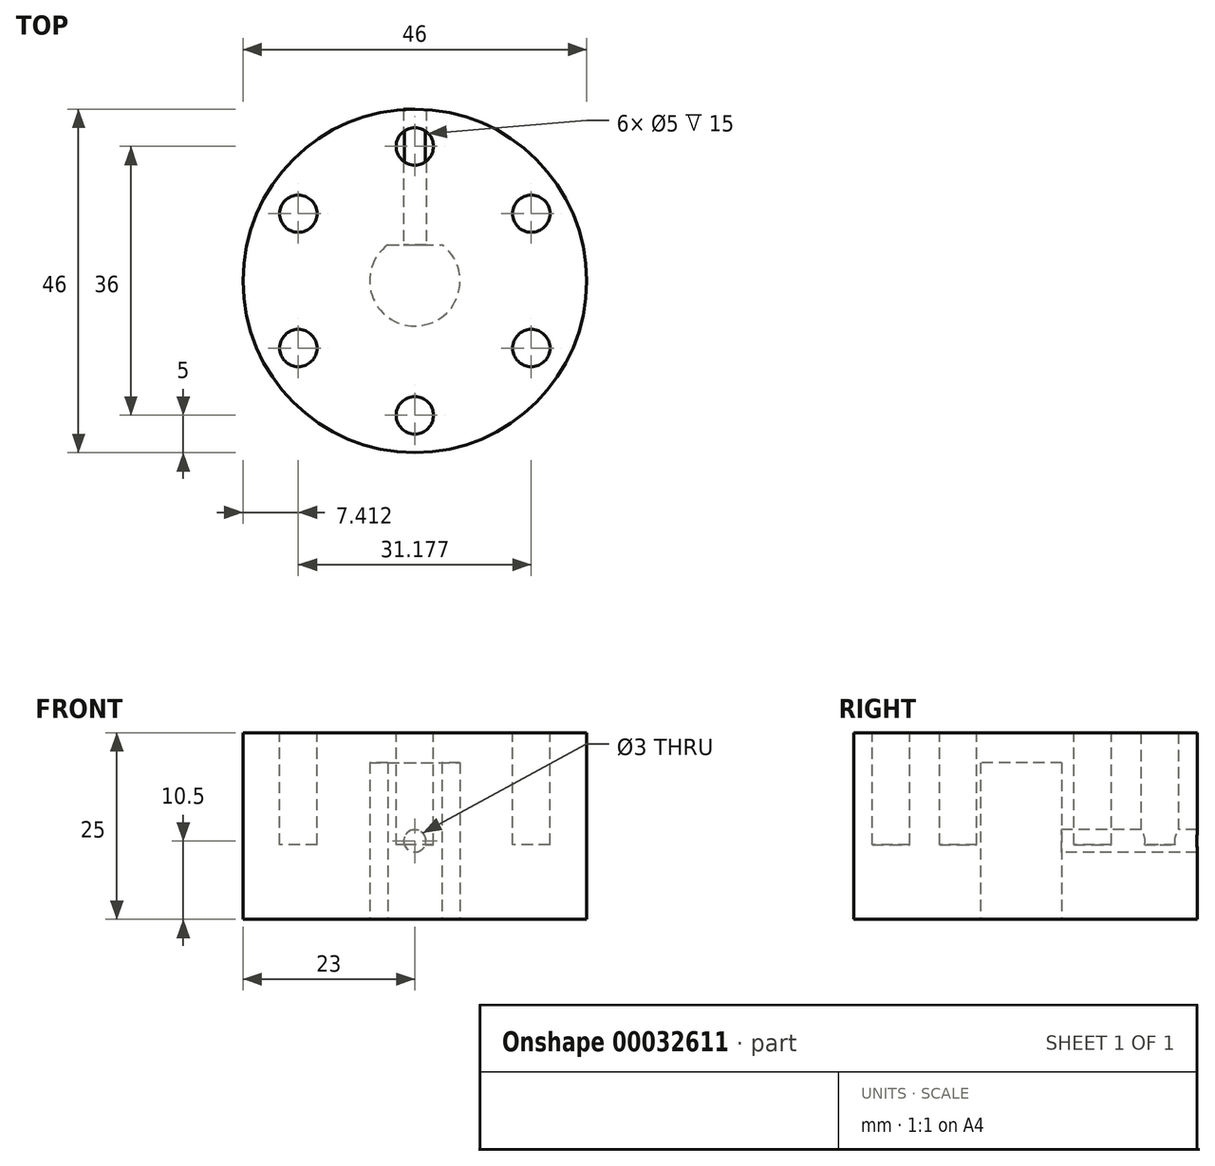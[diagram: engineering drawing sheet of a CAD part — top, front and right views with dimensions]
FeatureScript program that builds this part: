
annotation { "Feature Type Name" : "Feature", "Feature Type Description" : "" }
export const myFeature = defineFeature(function(context is Context, id is Id, definition is map)
    precondition{}
    {
        {
            var Q0;
            Q0=qCreatedBy(makeId("Top.planeOp"),FACE);
            var sketch = newSketch(context, id + "F0", { "sketchPlane" : qUnion([Q0])});
            skCircle(sketch, "E0", {"center": v(0, 0) * mm, "radius": 23 * mm});
            skCircle(sketch, "E1", {"center": v(0, 0) * mm, "radius": 6.05 * mm});
            skLineSegment(sketch, "E2.bottom", {"start": v(-4.85, 4.85) * mm, "end": v(4.85, 4.85) * mm});
            skLineSegment(sketch, "E2.top", {"start": v(-4.85, -4.85) * mm, "end": v(4.85, -4.85) * mm});
            skLineSegment(sketch, "E2.left", {"start": v(-4.85, 4.85) * mm, "end": v(-4.85, -4.85) * mm});
            skLineSegment(sketch, "E2.right", {"start": v(4.85, 4.85) * mm, "end": v(4.85, -4.85) * mm});
            skSolve(sketch);
        }
        {
            var Q0;
            {var subQ5=sQuery(id+"F0.wireOp",EDGE,"9920e3ed-193f-4a9b-bda4-b06f0bd62151.right");Q0=makeQuery(id+"F0.imprint","IMPRINT",FACE,{"disambiguationData":[TD([[makeQuery(id+"F0.imprint","IMPRINT",EDGE,{"derivedFrom":subQ5}),-1.0]])]});}
            var Q1;
            Q1=makeQuery(id+"F0.imprint","IMPRINT",FACE,{"disambiguationData":[TD([[makeQuery(id+"F0.imprint","IMPRINT",EDGE,{"derivedFrom":sQuery(id+"F0.wireOp",EDGE,"E0")}),1.0]])]});
            var Q2;
            {var subQ0=sQuery(id+"F0.wireOp",EDGE,"E2.bottom");var subQ1=sQuery(id+"F0.wireOp",EDGE,"E1");var subQ2=makeQuery(id+"F0.imprint","INTERSECT",VERTEX,{"disambiguationData":[OD(0.0)],"derivedFrom":[subQ1,subQ0]});Q2=makeQuery(id+"F0.imprint","IMPRINT",FACE,{"disambiguationData":[TD([[makeQuery(id+"F0.imprint","IMPRINT",EDGE,{"disambiguationData":[TD([[subQ2,1.0]])],"derivedFrom":subQ1}),-1.0]])]});}
            var Q3;
            {var subQ0=sQuery(id+"F0.wireOp",EDGE,"E2.bottom");var subQ1=sQuery(id+"F0.wireOp",EDGE,"E1");var subQ2=makeQuery(id+"F0.imprint","INTERSECT",VERTEX,{"disambiguationData":[OD(0.0)],"derivedFrom":[subQ1,subQ0]});Q3=makeQuery(id+"F0.imprint","IMPRINT",FACE,{"disambiguationData":[TD([[makeQuery(id+"F0.imprint","IMPRINT",EDGE,{"disambiguationData":[TD([[subQ2,-1.0]])],"derivedFrom":subQ1}),1.0]])]});}
            var Q4;
            {var subQ0=sQuery(id+"F0.wireOp",EDGE,"E2.bottom");var subQ1=sQuery(id+"F0.wireOp",EDGE,"E1");var subQ2=makeQuery(id+"F0.imprint","INTERSECT",VERTEX,{"disambiguationData":[OD(1.0)],"derivedFrom":[subQ1,subQ0]});Q4=makeQuery(id+"F0.imprint","IMPRINT",FACE,{"disambiguationData":[TD([[makeQuery(id+"F0.imprint","IMPRINT",EDGE,{"disambiguationData":[TD([[subQ2,-1.0]])],"derivedFrom":subQ1}),-1.0]])]});}
            var Q5;
            {var subQ0=sQuery(id+"F0.wireOp",EDGE,"E2.left");var subQ1=sQuery(id+"F0.wireOp",EDGE,"E1");var subQ2=makeQuery(id+"F0.imprint","INTERSECT",VERTEX,{"disambiguationData":[OD(1.0)],"derivedFrom":[subQ1,subQ0]});Q5=makeQuery(id+"F0.imprint","IMPRINT",FACE,{"disambiguationData":[TD([[makeQuery(id+"F0.imprint","IMPRINT",EDGE,{"disambiguationData":[TD([[subQ2,-1.0]])],"derivedFrom":subQ1}),-1.0]])]});}
            var Q6;
            {var subQ0=sQuery(id+"F0.wireOp",EDGE,"E2.top");var subQ1=sQuery(id+"F0.wireOp",EDGE,"E1");var subQ2=makeQuery(id+"F0.imprint","INTERSECT",VERTEX,{"disambiguationData":[OD(1.0)],"derivedFrom":[subQ1,subQ0]});Q6=makeQuery(id+"F0.imprint","IMPRINT",FACE,{"disambiguationData":[TD([[makeQuery(id+"F0.imprint","IMPRINT",EDGE,{"disambiguationData":[TD([[subQ2,-1.0]])],"derivedFrom":subQ1}),-1.0]])]});}
            extrude(context, id + "F4", {"entities" : qUnion([Q0, Q1, Q2, Q3, Q4, Q5, Q6]), "depth" : 25 * mm});
        }
        {
            var Q0;
            Q0=makeQuery(id+"F4.opExtrude","CAP_FACE",FACE,{"disambiguationData":[OSD([sQuery(id+"F0.wireOp",EDGE,"E0"),sQuery(id+"F0.wireOp",EDGE,"E1"),sQuery(id+"F0.wireOp",EDGE,"9920e3ed-193f-4a9b-bda4-b06f0bd62151.bottom"),sQuery(id+"F0.wireOp",EDGE,"9920e3ed-193f-4a9b-bda4-b06f0bd62151.top"),sQuery(id+"F0.wireOp",EDGE,"9920e3ed-193f-4a9b-bda4-b06f0bd62151.left")])],"isStart":false});
            var sketch = newSketch(context, id + "F5", { "sketchPlane" : qUnion([Q0])});
            skCircle(sketch, "E3", {"center": v(0, 0) * mm, "radius": 13.5 * mm});
            skSolve(sketch);
        }
        {
            var Q0;
            Q0=makeQuery(id+"F4.opExtrude","CAP_FACE",FACE,{"disambiguationData":[OSD([sQuery(id+"F0.wireOp",EDGE,"E0"),sQuery(id+"F0.wireOp",EDGE,"E1"),sQuery(id+"F0.wireOp",EDGE,"9920e3ed-193f-4a9b-bda4-b06f0bd62151.bottom"),sQuery(id+"F0.wireOp",EDGE,"9920e3ed-193f-4a9b-bda4-b06f0bd62151.top"),sQuery(id+"F0.wireOp",EDGE,"9920e3ed-193f-4a9b-bda4-b06f0bd62151.left")])],"isStart":false});
            var sketch = newSketch(context, id + "F6", { "sketchPlane" : qUnion([Q0])});
            skCircle(sketch, "E4.cCircle", {"center": v(0, 0) * mm, "radius": 15.59 * mm, "construction": true});
            skLineSegment(sketch, "E4.0", {"start": v(15.59, 9) * mm, "end": v(15.59, -9) * mm, "construction": true});
            skLineSegment(sketch, "E4.1", {"start": v(15.59, -9) * mm, "end": v(0, -18) * mm, "construction": true});
            skLineSegment(sketch, "E4.2", {"start": v(0, -18) * mm, "end": v(-15.59, -9) * mm, "construction": true});
            skLineSegment(sketch, "E4.3", {"start": v(-15.59, -9) * mm, "end": v(-15.59, 9) * mm, "construction": true});
            skLineSegment(sketch, "E4.4", {"start": v(-15.59, 9) * mm, "end": v(0, 18) * mm, "construction": true});
            skLineSegment(sketch, "E4.5", {"start": v(0, 18) * mm, "end": v(15.59, 9) * mm, "construction": true});
            skPoint(sketch, "E4.0.midPoint", {"position": v(15.59, 0) * mm});
            skCircle(sketch, "E5", {"center": v(15.59, 9) * mm, "radius": 2.5 * mm});
            skCircle(sketch, "E6", {"center": v(15.59, -9) * mm, "radius": 2.5 * mm});
            skCircle(sketch, "E7", {"center": v(0, -18) * mm, "radius": 2.5 * mm});
            skCircle(sketch, "E8", {"center": v(-15.59, -9) * mm, "radius": 2.5 * mm});
            skCircle(sketch, "E9", {"center": v(-15.59, 9) * mm, "radius": 2.5 * mm});
            skCircle(sketch, "E10", {"center": v(0, 18) * mm, "radius": 2.5 * mm});
            skSolve(sketch);
        }
        {
            var Q0;
            Q0=makeQuery(id+"F6.imprint","IMPRINT",FACE,{"disambiguationData":[TD([[makeQuery(id+"F6.imprint","IMPRINT",EDGE,{"derivedFrom":sQuery(id+"F6.wireOp",EDGE,"E5")}),1.0]])]});
            var Q1;
            Q1=makeQuery(id+"F6.imprint","IMPRINT",FACE,{"disambiguationData":[TD([[makeQuery(id+"F6.imprint","IMPRINT",EDGE,{"derivedFrom":sQuery(id+"F6.wireOp",EDGE,"E10")}),1.0]])]});
            var Q2;
            Q2=makeQuery(id+"F6.imprint","IMPRINT",FACE,{"disambiguationData":[TD([[makeQuery(id+"F6.imprint","IMPRINT",EDGE,{"derivedFrom":sQuery(id+"F6.wireOp",EDGE,"E9")}),1.0]])]});
            var Q3;
            Q3=makeQuery(id+"F6.imprint","IMPRINT",FACE,{"disambiguationData":[TD([[makeQuery(id+"F6.imprint","IMPRINT",EDGE,{"derivedFrom":sQuery(id+"F6.wireOp",EDGE,"E6")}),1.0]])]});
            var Q4;
            Q4=makeQuery(id+"F6.imprint","IMPRINT",FACE,{"disambiguationData":[TD([[makeQuery(id+"F6.imprint","IMPRINT",EDGE,{"derivedFrom":sQuery(id+"F6.wireOp",EDGE,"E7")}),1.0]])]});
            var Q5;
            Q5=makeQuery(id+"F6.imprint","IMPRINT",FACE,{"disambiguationData":[TD([[makeQuery(id+"F6.imprint","IMPRINT",EDGE,{"derivedFrom":sQuery(id+"F6.wireOp",EDGE,"E8")}),1.0]])]});
            extrude(context, id + "F1", {"entities" : qUnion([Q0, Q1, Q2, Q3, Q4, Q5]), "operationType" : NewBodyOperationType.REMOVE, "oppositeDirection" : true, "depth" : 15 * mm});
        }
        {
            var Q0;
            Q0=makeQuery(id+"F5.imprint","IMPRINT",FACE,{"disambiguationData":[TD([[makeQuery(id+"F5.imprint","IMPRINT",EDGE,{"derivedFrom":sQuery(id+"F5.wireOp",EDGE,"E3")}),1.0]])]});
            var sketch = newSketch(context, id + "F7", { "sketchPlane" : qUnion([Q0])});
            skArc(sketch, "E11.0", {"start": v(-3.62, 4.85) * mm, "mid": v(0, -6.05) * mm, "end": v(3.62, 4.85) * mm});
            skSolve(sketch);
        }
        {
            var Q0;
            Q0=makeQuery(id+"F7.imprint","IMPRINT",FACE,{"disambiguationData":[TD([[makeQuery(id+"F7.imprint","IMPRINT",EDGE,{"derivedFrom":sQuery(id+"F7.wireOp",EDGE,"E11.0")}),1.0]])]});
            extrude(context, id + "F2", {"entities" : qUnion([Q0]), "operationType" : NewBodyOperationType.ADD, "oppositeDirection" : true, "depth" : 4 * mm});
        }
        {
            var Q0;
            Q0=makeQuery(id+"F4.opExtrude","SWEPT_FACE",FACE,{"disambiguationData":[OSD([sQuery(id+"F0.wireOp",EDGE,"E2.bottom")])]});
            var sketch = newSketch(context, id + "F8", { "sketchPlane" : qUnion([Q0])});
            skCircle(sketch, "E12", {"center": v(0, 10.5) * mm, "radius": 1.5 * mm});
            skPoint(sketch, "E12.centerSnap0", {"position": v(3.62, 10.5) * mm});
            skSolve(sketch);
        }
        {
            var Q0;
            Q0=makeQuery(id+"F8.imprint","IMPRINT",FACE,{"disambiguationData":[TD([[makeQuery(id+"F8.imprint","IMPRINT",EDGE,{"derivedFrom":sQuery(id+"F8.wireOp",EDGE,"E12")}),1.0]])]});
            extrude(context, id + "F3", {"entities" : qUnion([Q0]), "operationType" : NewBodyOperationType.REMOVE, "oppositeDirection" : true, "depth" : 35 * mm});
        }
    });
